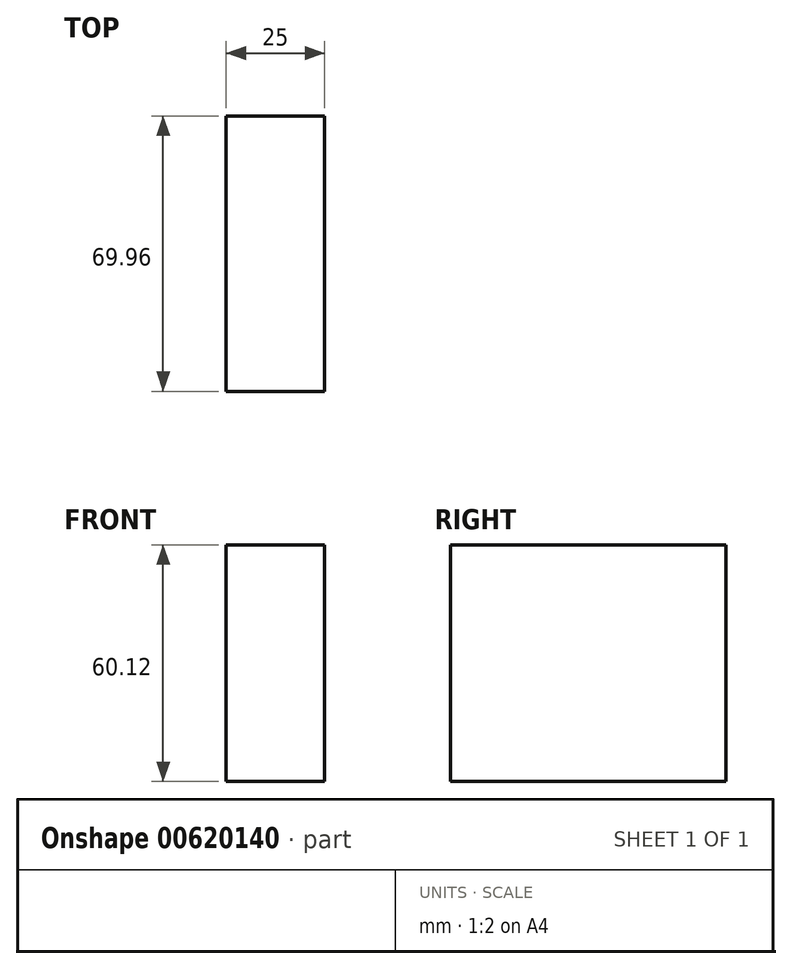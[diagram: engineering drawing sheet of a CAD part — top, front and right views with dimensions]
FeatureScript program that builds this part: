
annotation { "Feature Type Name" : "Feature", "Feature Type Description" : "" }
export const myFeature = defineFeature(function(context is Context, id is Id, definition is map)
    precondition{}
    {
        {
            var Q0;
            Q0=qCreatedBy(makeId("Right.planeOp"),FACE);
            var sketch = newSketch(context, id + "F0", { "sketchPlane" : qUnion([Q0])});
            skLineSegment(sketch, "E0.bottom", {"start": v(-123.29, 15.18) * mm, "end": v(-53.33, 15.18) * mm});
            skLineSegment(sketch, "E0.top", {"start": v(-123.29, 75.3) * mm, "end": v(-53.33, 75.3) * mm});
            skLineSegment(sketch, "E0.left", {"start": v(-123.29, 15.18) * mm, "end": v(-123.29, 75.3) * mm});
            skLineSegment(sketch, "E0.right", {"start": v(-53.33, 15.18) * mm, "end": v(-53.33, 75.3) * mm});
            skPoint(sketch, "E0.middle", {"position": v(-88.31, 45.24) * mm});
            skSolve(sketch);
        }
        {
            var Q0;
            Q0=makeQuery(id+"F0.imprint","IMPRINT",FACE,{"disambiguationData":[TD([[makeQuery(id+"F0.imprint","IMPRINT",EDGE,{"derivedFrom":sQuery(id+"F0.wireOp",EDGE,"E0.bottom")}),1.0]])]});
            extrude(context, id + "F1", {"entities" : qUnion([Q0]), "depth" : 25 * mm, "offsetDistance" : 25 * mm});
        }
    });
